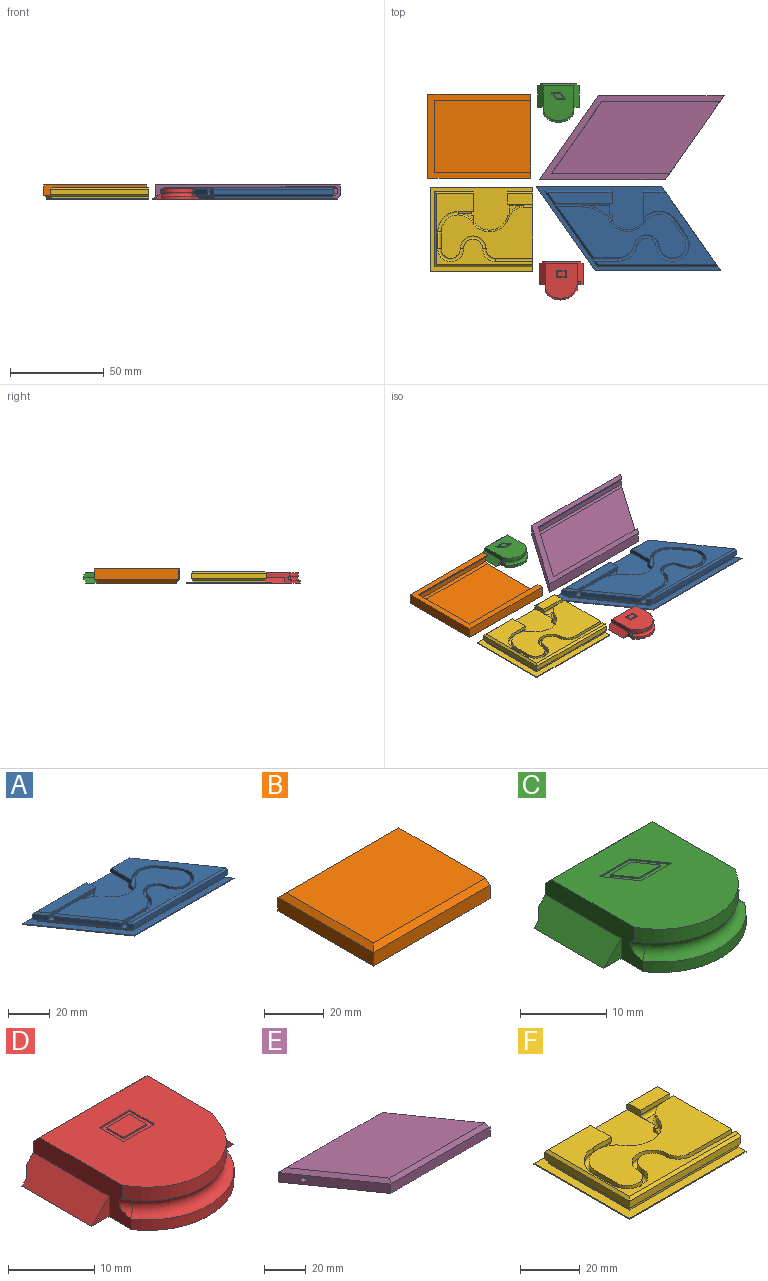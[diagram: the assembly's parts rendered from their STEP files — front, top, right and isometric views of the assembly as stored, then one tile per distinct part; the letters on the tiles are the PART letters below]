
ASSEMBLY  parts=6 mates=5
PART A: 63 faces, bbox 98.7x45x6 mm
  f0: torus R=18.89mm, axis (0,0,-1), area 51.9mm2, adj f22,f39,f41,f62
  f1: plane 34.05x5.7mm, normal (0,0,1), area 182.7mm2, adj f11,f21,f48,f53
  f2: plane 3.5x1.6mm, normal (1,0,0), area 5.6mm2, adj f12,f13,f14,f62
  f3: plane 45x31.51mm, normal (0.82,0.57,0), area 292.4mm2, adj f4,f5,f8,f9,f13,f54,f55,f56
  f4: plane 64.18x38.2mm, normal (0,0,1), area 625.8mm2, adj f3,f10,f18,f24,f26,f29,f32,f35
  f5: plane 67.14x0.4mm, normal (0,1,0), area 26.9mm2, adj f3,f7,f9,f13
  f6: plane 68.3x27.2mm, normal (0,0,1), area 998.6mm2, adj f20,f23,f28,f31,f34,f37,f38,f40
  f7: plane 45x31.51mm, normal (-0.82,-0.57,0), area 22mm2, adj f5,f8,f9,f13
  f8: plane 67.14x0.4mm, normal (0,-1,0), area 26.9mm2, adj f3,f7,f9,f13
  f9: plane 98.65x45mm, normal (0,0,-1), area 3021.4mm2, adj f3,f5,f7,f8
  f10: plane 16.1x5.6mm, normal (-1,0,0), area 45.4mm2, adj f4,f12,f13,f16,f17,f24,f25,f58
  f11: plane 6.7x2.6mm, normal (1,0,0), area 16.8mm2, adj f1,f15,f21,f22,f52,f53
  f12: cylinder r=10mm len=16.7mm, axis (0,0,-1), area 31.6mm2, adj f2,f10,f13,f39
  f13: plane 98.65x45mm, normal (0,0,1), area 989.9mm2, adj f2,f3,f5,f7,f8,f10,f12,f14
  f14: plane 3x1.6mm, normal (0,1,0), area 3.5mm2, adj f2,f13,f15,f62
  f15: plane 12.6x3mm, normal (0.71,0,-0.71), area 39.7mm2, adj f11,f13,f14,f22,f43,f51,f52,f62
  f16: plane 3x3mm, normal (0,1,0), area 4.5mm2, adj f10,f13,f17
  f17: plane 12.6x3mm, normal (-0.71,0,-0.71), area 51.6mm2, adj f10,f13,f16,f59,f60,f61
  f18: plane 12.64x1.88mm, normal (0,1,0), area 23.2mm2, adj f4,f19,f26,f49,f50
  f19: cylinder r=1.25mm len=14.15mm, axis (-1,0,0), area 77.3mm2, adj f18,f20,f27,f45,f46,f49
  f20: plane 13.9x1.88mm, normal (0,-1,0), area 25.6mm2, adj f6,f19,f28,f44,f45
  f21: plane 31.28x1.88mm, normal (0,-1,0), area 58.3mm2, adj f1,f11,f22,f47,f48
  f22: cylinder r=1.25mm len=31.52mm, axis (1,0,0), area 130.9mm2, adj f0,f11,f15,f21,f23,f45,f46,f47
  f23: plane 14.24x1.88mm, normal (0,1,0), area 26.2mm2, adj f6,f22,f41,f44,f45
  f24: cylinder r=10.9mm len=17.28mm, axis (0,0,-1), area 37.6mm2, adj f4,f10,f25,f35
  f25: torus R=10mm, axis (0,0,-1), area 110.2mm2, adj f10,f24,f36,f38,f39
  f26: cylinder r=10.9mm len=10.61mm, axis (0,0,-1), area 27.5mm2, adj f4,f18,f27,f29
  f27: torus R=10mm, axis (0,0,-1), area 78.2mm2, adj f19,f26,f28,f30
  f28: cylinder r=9.1mm len=8.86mm, axis (0,0,-1), area 22.9mm2, adj f6,f20,f27,f31
  f29: cylinder r=5.1mm len=10.03mm, axis (0,0,1), area 26.8mm2, adj f4,f26,f30,f32
  f30: torus R=6mm, axis (0,0,1), area 97.8mm2, adj f27,f29,f31,f33
  f31: cylinder r=6.9mm len=13.57mm, axis (0,0,1), area 36.2mm2, adj f6,f28,f30,f34
  f32: cylinder r=8.9mm len=17.74mm, axis (0,0,-1), area 60.9mm2, adj f4,f29,f33,f35
  f33: torus R=8mm, axis (0,0,-1), area 169.8mm2, adj f30,f32,f34,f36
  f34: cylinder r=7.1mm len=14.15mm, axis (0,0,-1), area 48.5mm2, adj f6,f31,f33,f37
  f35: plane 8.15x5.7mm, normal (-0.82,-0.57,0), area 18.7mm2, adj f4,f24,f32,f36
  f36: cylinder r=1.25mm len=9.58mm, axis (0.57,-0.82,0), area 58.1mm2, adj f25,f33,f35,f37
  f37: plane 8.15x5.7mm, normal (0.82,0.57,0), area 18.7mm2, adj f6,f34,f36,f38
  f38: cylinder r=9.1mm len=15.05mm, axis (0,0,-1), area 33.4mm2, adj f6,f25,f37,f40
  f39: torus R=10mm, axis (0,0,1), area 63mm2, adj f0,f12,f25,f40
  f40: cylinder r=10.9mm len=18.21mm, axis (0,0,1), area 40.6mm2, adj f6,f38,f39,f41
  f41: cylinder r=17.99mm len=15.02mm, axis (0,0,-1), area 33.5mm2, adj f0,f6,f23,f40
  f42: plane 38.2x26.75mm, normal (-0.82,-0.57,0), area 37.3mm2, adj f13,f43,f46,f54
  f43: plane 31.85x0.8mm, normal (0,1,0), area 25.2mm2, adj f13,f15,f42,f51
  f44: plane 27.2x20.27mm, normal (-0.58,-0.41,0.71), area 47mm2, adj f6,f20,f23,f45
  f45: plane 27.64x19.36mm, normal (-0.82,-0.57,0), area 92mm2, adj f19,f20,f22,f23,f44,f46
  f46: plane 40.2x28.67mm, normal (-0.58,-0.41,-0.71), area 67mm2, adj f19,f22,f42,f45,f47,f49,f51,f55
  f47: plane 6.92x4.85mm, normal (-0.82,-0.57,0), area 22.4mm2, adj f21,f22,f46,f48,f52
  f48: plane 6.7x5.91mm, normal (-0.58,-0.41,0.71), area 10.7mm2, adj f1,f21,f47,f53
  f49: plane 2.92x2.8mm, normal (-0.82,-0.57,0), area 8.7mm2, adj f18,f19,f46,f50,f56
  f50: plane 2.7x2.41mm, normal (-0.58,-0.41,0.71), area 3.8mm2, adj f4,f18,f49,f57
  f51: plane 34.77x1mm, normal (0,0.71,-0.71), area 47.1mm2, adj f15,f43,f46,f52
  f52: plane 35.97x2.8mm, normal (0,1,0), area 100mm2, adj f11,f15,f47,f51,f53
  f53: plane 35.97x1mm, normal (0,0.71,0.71), area 49.5mm2, adj f1,f11,f48,f52
  f54: plane 62.99x0.8mm, normal (0,-1,0), area 50.4mm2, adj f3,f13,f42,f55
  f55: plane 64.21x1mm, normal (0,-0.71,-0.71), area 89.9mm2, adj f3,f46,f54,f56
  f56: plane 64.21x2.8mm, normal (0,-1,0), area 179.8mm2, adj f3,f49,f55,f57
  f57: plane 64.21x1mm, normal (0,-0.71,0.71), area 89.9mm2, adj f3,f4,f50,f56
  f58: plane 12.24x1mm, normal (0,0.71,0.71), area 16.8mm2, adj f3,f4,f10,f59
  f59: plane 11.54x2.8mm, normal (0,1,0), area 31.6mm2, adj f3,f10,f17,f58,f60
  f60: plane 11.04x1mm, normal (0,0.71,-0.71), area 14.4mm2, adj f3,f17,f59,f61
  f61: plane 10.04x0.8mm, normal (0,1,0), area 7.7mm2, adj f3,f13,f17,f60
  f62: plane 15.78x8.5mm, normal (0,0,1), area 32.7mm2, adj f0,f2,f14,f15,f22
PART B: 22 faces, bbox 55x45x7.5 mm
  f0: plane 45x7.5mm, normal (1,0,0), area 110.7mm2, adj f1,f2,f3,f4,f5,f11,f12,f13
  f1: plane 55x5.5mm, normal (0,-1,0), area 302.5mm2, adj f0,f6,f12,f21
  f2: plane 51.7x0.66mm, normal (0,1,0), area 34mm2, adj f0,f3,f7,f12
  f3: plane 52.7x1mm, normal (0,0.71,0.71), area 73.8mm2, adj f0,f2,f4,f8
  f4: plane 52.7x2.88mm, normal (0,1,0), area 151.9mm2, adj f0,f3,f5,f9
  f5: plane 52.7x1.06mm, normal (0,0.71,-0.71), area 78.1mm2, adj f0,f4,f10,f18
  f6: plane 45x5.5mm, normal (-1,0,0), area 247.5mm2, adj f1,f11,f12,f20
  f7: plane 38.4x0.66mm, normal (1,0,0), area 25.3mm2, adj f2,f8,f12,f13
  f8: plane 40.4x1mm, normal (0.71,0,0.71), area 55.7mm2, adj f3,f7,f9,f14
  f9: plane 40.4x2.88mm, normal (1,0,0), area 116.5mm2, adj f4,f8,f10,f15
  f10: plane 40.4x1.06mm, normal (0.71,0,-0.71), area 58.9mm2, adj f5,f9,f16,f18
  f11: plane 55x5.5mm, normal (0,1,0), area 302.5mm2, adj f0,f6,f12,f19
  f12: plane 55x45mm, normal (0,0,-1), area 489.7mm2, adj f0,f1,f2,f6,f7,f11,f13
  f13: plane 51.7x0.66mm, normal (0,-1,0), area 34mm2, adj f0,f7,f12,f14
  f14: plane 52.7x1mm, normal (0,-0.71,0.71), area 73.8mm2, adj f0,f8,f13,f15
  f15: plane 52.7x2.88mm, normal (0,-1,0), area 151.9mm2, adj f0,f9,f14,f16
  f16: plane 52.7x1.06mm, normal (0,-0.71,-0.71), area 78.1mm2, adj f0,f10,f15,f18
  f17: plane 53x41mm, normal (0,0,1), area 2173mm2, adj f0,f19,f20,f21
  f18: plane 51.64x38.28mm, normal (0,0,-1), area 1977mm2, adj f0,f5,f10,f16
  f19: plane 55x2mm, normal (0,0.71,0.71), area 152.7mm2, adj f0,f11,f17,f20
  f20: plane 45x2mm, normal (-0.71,0,0.71), area 121.6mm2, adj f6,f17,f19,f21
  f21: plane 55x2mm, normal (0,-0.71,0.71), area 152.7mm2, adj f0,f1,f17,f20
PART C: 29 faces, bbox 22.2x22.3x5.5 mm
  f0: plane 18.56x16.5mm, normal (0,0,1), area 261.9mm2, adj f1,f2,f10,f12,f13,f18,f22,f23
  f1: plane 16.15x5.5mm, normal (1,0,0), area 46.2mm2, adj f0,f3,f4,f7,f8,f9,f10,f11
  f2: plane 16.15x5.5mm, normal (-1,0,0), area 46mm2, adj f0,f3,f4,f5,f6,f9,f13,f14
  f3: cylinder r=10mm len=16.5mm, axis (0,0,-1), area 29.1mm2, adj f1,f2,f4,f9
  f4: plane 22.22x19.5mm, normal (0,0,-1), area 365.6mm2, adj f1,f2,f3,f5,f6,f7,f8,f16
  f5: plane 2.86x2.86mm, normal (0,-1,0), area 4.1mm2, adj f2,f4,f6
  f6: plane 12.4x2.86mm, normal (-0.71,0,0.71), area 48.4mm2, adj f2,f4,f5,f15,f16,f17
  f7: plane 2.86x2.86mm, normal (0,-1,0), area 4.1mm2, adj f1,f4,f8
  f8: plane 12.4x2.86mm, normal (0.71,0,0.71), area 48.4mm2, adj f1,f4,f7,f15,f16,f17
  f9: torus R=10mm, axis (0,0,1), area 52.5mm2, adj f1,f2,f3,f11,f12,f14
  f10: cylinder r=10.9mm len=1.88mm, axis (0,0,-1), area 2.1mm2, adj f0,f1,f11,f12
  f11: torus R=10mm, axis (0,0,-1), area 3.2mm2, adj f1,f9,f10
  f12: cylinder r=9.1mm len=15.2mm, axis (0,0,1), area 33.9mm2, adj f0,f9,f10,f13
  f13: cylinder r=19.79mm len=1.88mm, axis (0,0,-1), area 2.1mm2, adj f0,f2,f12,f14
  f14: torus R=18.89mm, axis (0,0,-1), area 3.3mm2, adj f2,f9,f13
  f15: plane 20.74x1mm, normal (0,0.71,-0.71), area 27.9mm2, adj f6,f8,f16,f17
  f16: plane 22.22x0.74mm, normal (0,1,0), area 15.9mm2, adj f4,f6,f8,f15
  f17: plane 18.74x2.72mm, normal (0,1,0), area 46.1mm2, adj f1,f2,f6,f8,f15,f18
  f18: plane 16.5x1.04mm, normal (0,0.71,0.71), area 24.3mm2, adj f0,f1,f2,f17
  f19: plane 3.54x0.2mm, normal (0,1,0), area 0.7mm2, adj f20,f26,f27,f28
  f20: plane 2.8x1.96mm, normal (0.82,0.57,0), area 0.7mm2, adj f19,f21,f27,f28
  f21: plane 3.54x0.2mm, normal (0,-1,0), area 0.7mm2, adj f20,f26,f27,f28
  f22: plane 5x0.2mm, normal (0,-1,0), area 1mm2, adj f0,f23,f25,f27
  f23: plane 4x2.8mm, normal (0.82,0.57,0), area 1mm2, adj f0,f22,f24,f27
  f24: plane 5x0.2mm, normal (0,1,0), area 1mm2, adj f0,f23,f25,f27
  f25: plane 4x2.8mm, normal (-0.82,-0.57,0), area 1mm2, adj f0,f22,f24,f27
  f26: plane 2.8x1.96mm, normal (-0.82,-0.57,0), area 0.7mm2, adj f19,f21,f27,f28
  f27: plane 7.8x4mm, normal (0,0,1), area 10.1mm2, adj f19,f20,f21,f22,f23,f24,f25,f26
  f28: plane 5.5x2.8mm, normal (0,0,1), area 9.9mm2, adj f19,f20,f21,f26
PART D: 30 faces, bbox 23.5x22.5x5.7 mm
  f0: plane 18.56x17.59mm, normal (0,0,1), area 274.9mm2, adj f3,f4,f11,f13,f14,f19,f20,f21
  f1: plane 23.31x19.5mm, normal (0,0,-1), area 381.1mm2, adj f2,f4,f5,f6,f7,f8,f9,f16
  f2: plane 1.75x1.74mm, normal (1,0,0), area 2.6mm2, adj f1,f5,f8,f10,f12
  f3: plane 12.03x2.84mm, normal (1,0,0), area 30.4mm2, adj f0,f9,f11,f12,f18,f19
  f4: plane 16.15x5.5mm, normal (-1,0,0), area 46.2mm2, adj f0,f1,f5,f6,f7,f10,f14,f15
  f5: cylinder r=10mm len=17.59mm, axis (0,0,-1), area 32.7mm2, adj f1,f2,f4,f10
  f6: plane 2.86x2.86mm, normal (0,-1,0), area 4.1mm2, adj f1,f4,f7
  f7: plane 12.4x2.86mm, normal (-0.71,0,0.71), area 48.4mm2, adj f1,f4,f6,f16,f17,f18
  f8: plane 2.91x1.72mm, normal (0,-1,0), area 3.2mm2, adj f1,f2,f9,f12
  f9: plane 12.4x2.86mm, normal (0.71,0,0.71), area 45mm2, adj f1,f3,f8,f12,f16,f17,f18
  f10: torus R=10mm, axis (0,0,1), area 59.1mm2, adj f2,f4,f5,f12,f13,f15
  f11: cylinder r=10.28mm len=1.88mm, axis (0,0,-1), area 3.4mm2, adj f0,f3,f12,f13
  f12: torus R=9.38mm, axis (0,0,-1), area 8.3mm2, adj f2,f3,f8,f9,f10,f11
  f13: cylinder r=9.1mm len=16.19mm, axis (0,0,1), area 38.1mm2, adj f0,f10,f11,f14
  f14: cylinder r=10.9mm len=1.88mm, axis (0,0,-1), area 2.1mm2, adj f0,f4,f13,f15
  f15: torus R=10mm, axis (0,0,-1), area 3.2mm2, adj f4,f10,f14
  f16: plane 23.31x0.74mm, normal (0,1,0), area 16.7mm2, adj f1,f7,f9,f17
  f17: plane 21.83x1mm, normal (0,0.71,-0.71), area 29.5mm2, adj f7,f9,f16,f18
  f18: plane 19.83x2.72mm, normal (0,1,0), area 49.1mm2, adj f3,f4,f7,f9,f17,f19
  f19: plane 17.59x1.04mm, normal (0,0.71,0.71), area 25.9mm2, adj f0,f3,f4,f18
  f20: plane 5x0.2mm, normal (0,-1,0), area 1mm2, adj f0,f21,f27,f28
  f21: plane 4x0.2mm, normal (1,0,0), area 0.8mm2, adj f0,f20,f22,f28
  f22: plane 5x0.2mm, normal (0,1,0), area 1mm2, adj f0,f21,f27,f28
  f23: plane 3.8x0.2mm, normal (0,1,0), area 0.8mm2, adj f24,f26,f28,f29
  f24: plane 2.8x0.2mm, normal (1,0,0), area 0.6mm2, adj f23,f25,f28,f29
  f25: plane 3.8x0.2mm, normal (0,-1,0), area 0.8mm2, adj f24,f26,f28,f29
  f26: plane 2.8x0.2mm, normal (-1,0,0), area 0.6mm2, adj f23,f25,f28,f29
  f27: plane 4x0.2mm, normal (-1,0,0), area 0.8mm2, adj f0,f20,f22,f28
  f28: plane 5x4mm, normal (0,0,1), area 9.4mm2, adj f20,f21,f22,f23,f24,f25,f26,f27
  f29: plane 3.8x2.8mm, normal (0,0,1), area 10.6mm2, adj f23,f24,f25,f26
PART E: 23 faces, bbox 98.7x45x7.5 mm
  f0: plane 64.34x2.88mm, normal (0,-1,0), area 185.5mm2, adj f1,f3,f11,f16
  f1: plane 65.04x1mm, normal (0,-0.71,0.71), area 90.1mm2, adj f0,f2,f12,f16
  f2: plane 63.11x0.66mm, normal (0,-1,0), area 41.6mm2, adj f1,f7,f13,f16
  f3: plane 65.08x1.06mm, normal (0,-0.71,-0.71), area 95.3mm2, adj f0,f14,f16,f17
  f4: plane 64.34x2.88mm, normal (0,1,0), area 185.5mm2, adj f5,f8,f11,f16
  f5: plane 64.34x1mm, normal (0,0.71,0.71), area 90.1mm2, adj f4,f6,f12,f16
  f6: plane 63.11x0.66mm, normal (0,1,0), area 41.6mm2, adj f5,f7,f13,f16
  f7: plane 98.65x45mm, normal (0,0,-1), area 597.8mm2, adj f2,f6,f9,f10,f13,f15,f16
  f8: plane 64.34x1.06mm, normal (0,0.71,-0.71), area 95.3mm2, adj f4,f14,f16,f17
  f9: plane 67.14x5.5mm, normal (0,1,0), area 369.3mm2, adj f7,f10,f16,f19
  f10: plane 45x31.51mm, normal (-0.82,-0.57,0), area 296.1mm2, adj f7,f9,f15,f20,f22
  f11: plane 40.4x28.29mm, normal (0.82,0.57,0), area 136.3mm2, adj f0,f4,f12,f14,f22
  f12: plane 40.4x28.81mm, normal (0.58,0.41,0.71), area 67.8mm2, adj f1,f5,f11,f13,f22
  f13: plane 38.4x26.89mm, normal (0.82,0.57,0), area 30.9mm2, adj f2,f6,f7,f12
  f14: plane 40.4x28.84mm, normal (0.58,0.41,-0.71), area 71.9mm2, adj f3,f8,f11,f17
  f15: plane 67.14x5.5mm, normal (0,-1,0), area 369.3mm2, adj f7,f10,f16,f21
  f16: plane 45x31.51mm, normal (0.82,0.57,0), area 135.1mm2, adj f0,f1,f2,f3,f4,f5,f6,f7
  f17: plane 89.85x38.28mm, normal (0,0,-1), area 2413.4mm2, adj f3,f8,f14,f16
  f18: plane 93.41x41mm, normal (0,0,1), area 2652.7mm2, adj f16,f19,f20,f21
  f19: plane 68.54x2mm, normal (0,0.71,0.71), area 186.5mm2, adj f9,f16,f18,f20
  f20: plane 45x32.55mm, normal (-0.58,-0.41,0.71), area 148.5mm2, adj f10,f18,f19,f21
  f21: plane 67.14x2mm, normal (0,-0.71,0.71), area 186.5mm2, adj f15,f16,f18,f20
  f22: cylinder r=1.25mm len=4.56mm, axis (-1,0,0), area 22.2mm2, adj f10,f11,f12
PART F: 64 faces, bbox 55.1x45.1x6.1 mm
  f0: torus R=10mm, axis (0,0,-1), area 118.1mm2, adj f2,f6,f29,f31,f33,f61
  f1: torus R=9.38mm, axis (0,0,-1), area 30.1mm2, adj f20,f21,f26,f28,f29,f62,f63
  f2: cylinder r=1.25mm len=8.35mm, axis (1,0,0), area 22.5mm2, adj f0,f5,f19,f60,f61
  f3: plane 13.85x5.7mm, normal (0,0,1), area 79mm2, adj f8,f14,f25,f47
  f4: plane 51.6x38.2mm, normal (0,0,1), area 467.4mm2, adj f5,f6,f8,f22,f32,f35,f38,f41
  f5: plane 10.7x2.6mm, normal (1,0,0), area 27.2mm2, adj f2,f4,f19,f48,f49,f60
  f6: cylinder r=10.9mm len=10.9mm, axis (0,0,-1), area 32.2mm2, adj f0,f4,f32,f60
  f7: plane 55x0.4mm, normal (0,1,0), area 22mm2, adj f8,f11,f13,f17
  f8: plane 45x6mm, normal (1,0,0), area 223.9mm2, adj f3,f4,f7,f9,f11,f12,f17,f22
  f9: plane 49.1x27.2mm, normal (0,0,1), area 848.9mm2, adj f8,f24,f27,f28,f30,f31,f34,f37
  f10: plane 1.6x1.29mm, normal (-1,0,0), area 2.1mm2, adj f16,f17,f20,f63
  f11: plane 55x45mm, normal (0,0,-1), area 2475mm2, adj f7,f8,f12,f13
  f12: plane 55x0.4mm, normal (0,-1,0), area 22mm2, adj f8,f11,f13,f17
  f13: plane 45x0.4mm, normal (-1,0,0), area 18mm2, adj f7,f11,f12,f17
  f14: plane 6.7x2.6mm, normal (-1,0,0), area 16.8mm2, adj f3,f21,f25,f26,f44,f47
  f15: plane 3.5x1.6mm, normal (1,0,0), area 5.6mm2, adj f16,f17,f18,f61
  f16: cylinder r=10mm len=17.79mm, axis (0,0,-1), area 35.6mm2, adj f10,f15,f17,f29
  f17: plane 55x45mm, normal (0,0,1), area 894mm2, adj f7,f8,f10,f12,f13,f15,f16,f18
  f18: plane 3x1.6mm, normal (0,1,0), area 3.5mm2, adj f15,f17,f19,f61
  f19: plane 12.6x3mm, normal (0.71,0,-0.71), area 47.6mm2, adj f2,f5,f17,f18,f49,f58,f59,f61
  f20: plane 3x1.76mm, normal (0,1,0), area 3.6mm2, adj f1,f10,f17,f21,f63
  f21: plane 12.7x3.1mm, normal (-0.71,0,-0.71), area 39.8mm2, adj f1,f14,f17,f20,f26,f44,f45,f46
  f22: plane 20x1.88mm, normal (0,1,0), area 37.7mm2, adj f4,f8,f23,f41
  f23: cylinder r=1.25mm len=20mm, axis (-1,0,0), area 116.9mm2, adj f8,f22,f24,f42
  f24: plane 20x1.88mm, normal (0,-1,0), area 37.7mm2, adj f8,f9,f23,f43
  f25: plane 13.85x1.88mm, normal (0,-1,0), area 26.1mm2, adj f3,f8,f14,f26
  f26: cylinder r=1.25mm len=13.85mm, axis (1,0,0), area 53.2mm2, adj f1,f8,f14,f21,f25,f27,f62
  f27: plane 5x1.88mm, normal (0,1,0), area 9.4mm2, adj f8,f9,f26,f28
  f28: cylinder r=8.48mm len=8mm, axis (0,0,-1), area 19.7mm2, adj f1,f9,f27,f30
  f29: torus R=10mm, axis (0,0,1), area 70.9mm2, adj f0,f1,f16,f30
  f30: cylinder r=10.9mm len=19.4mm, axis (0,0,1), area 45.6mm2, adj f9,f28,f29,f31
  f31: cylinder r=9.1mm len=16.7mm, axis (0,0,-1), area 43.8mm2, adj f0,f9,f30,f34
  f32: plane 9x1.88mm, normal (1,0,0), area 16.9mm2, adj f4,f6,f33,f35
  f33: cylinder r=1.25mm len=9mm, axis (0,1,0), area 52.6mm2, adj f0,f32,f34,f36
  f34: plane 9x1.88mm, normal (-1,0,0), area 16.9mm2, adj f9,f31,f33,f37
  f35: cylinder r=6.9mm len=13.8mm, axis (0,0,-1), area 40.8mm2, adj f4,f32,f36,f38
  f36: torus R=6mm, axis (0,0,-1), area 110.2mm2, adj f33,f35,f37,f39
  f37: cylinder r=5.1mm len=10.2mm, axis (0,0,-1), area 30.2mm2, adj f9,f34,f36,f40
  f38: cylinder r=5.1mm len=10.2mm, axis (0,0,1), area 30.2mm2, adj f4,f35,f39,f41
  f39: torus R=6mm, axis (0,0,1), area 110.2mm2, adj f36,f38,f40,f42
  f40: cylinder r=6.9mm len=13.8mm, axis (0,0,1), area 40.8mm2, adj f9,f37,f39,f43
  f41: cylinder r=6.9mm len=6.9mm, axis (0,0,-1), area 20.4mm2, adj f4,f22,f38,f42
  f42: torus R=6mm, axis (0,0,-1), area 55.1mm2, adj f23,f39,f41,f43
  f43: cylinder r=5.1mm len=5.1mm, axis (0,0,-1), area 15.1mm2, adj f9,f24,f40,f42
  f44: plane 13.85x2.8mm, normal (0,1,0), area 38.1mm2, adj f8,f14,f21,f45,f47
  f45: plane 12.65x1mm, normal (0,0.71,-0.71), area 17.2mm2, adj f8,f21,f44,f46
  f46: plane 11.65x0.8mm, normal (0,1,0), area 9mm2, adj f8,f17,f21,f45
  f47: plane 13.85x1mm, normal (0,0.71,0.71), area 19.6mm2, adj f3,f8,f14,f44
  f48: plane 20.95x1mm, normal (0,0.71,0.71), area 28.9mm2, adj f4,f5,f49,f57
  f49: plane 20.95x2.8mm, normal (0,1,0), area 57.9mm2, adj f5,f19,f48,f56,f59
  f50: plane 51.6x0.8mm, normal (0,-1,0), area 41.3mm2, adj f8,f17,f51,f54
  f51: plane 52.6x1mm, normal (0,-0.71,-0.71), area 73.7mm2, adj f8,f50,f52,f55
  f52: plane 52.6x2.8mm, normal (0,-1,0), area 147.3mm2, adj f8,f51,f53,f56
  f53: plane 52.6x1mm, normal (0,-0.71,0.71), area 73.7mm2, adj f4,f8,f52,f57
  f54: plane 38.2x0.8mm, normal (-1,0,0), area 30.6mm2, adj f17,f50,f55,f58
  f55: plane 40.2x1mm, normal (-0.71,0,-0.71), area 55.4mm2, adj f51,f54,f56,f59
  f56: plane 40.2x2.8mm, normal (-1,0,0), area 112.6mm2, adj f49,f52,f55,f57
  f57: plane 40.2x1mm, normal (-0.71,0,0.71), area 55.4mm2, adj f4,f48,f53,f56
  f58: plane 17.75x0.8mm, normal (0,1,0), area 13.9mm2, adj f17,f19,f54,f59
  f59: plane 19.75x1mm, normal (0,0.71,-0.71), area 26.5mm2, adj f19,f49,f55,f58
  f60: plane 8.35x1.88mm, normal (0,-1,0), area 15.7mm2, adj f2,f4,f5,f6
  f61: plane 8.35x4.5mm, normal (0,0,1), area 9.7mm2, adj f0,f2,f15,f18,f19
  f62: plane 7.45x3.69mm, normal (0,0,1), area 8.3mm2, adj f1,f21,f26
  f63: plane 1.29x0.56mm, normal (0,0,1), area 0.3mm2, adj f1,f10,f20
PLACE A t=(1.65,0.25,0)mm
PLACE B rot(axis=(1,0,0),180deg) t=(-1.15,49.67,8)mm
PLACE C t=(-35.32,57.58,-0.5)mm
PLACE D t=(37.96,-37.35,-0.5)mm
PLACE E rot(axis=(1,0,0),180deg) t=(3.45,48.86,8)mm
PLACE F at identity fixed
MATE planar F.f11 <-> A.f9  axis (0,0,-1) through (-27.5,0,0)mm
MATE planar E.f18 <-> A.f9  axis (0,0,-1) through (54,48.86,0)mm
MATE planar C.f3 <-> F.f11  axis (0,0,-1) through (13.61,67.08,0)mm
MATE planar D.f1 <-> F.f11  axis (0,0,-1) through (15.12,-26.82,0)mm
MATE planar B.f17 <-> F.f11  axis (0,0,-1) through (-27.65,49.67,0)mm
